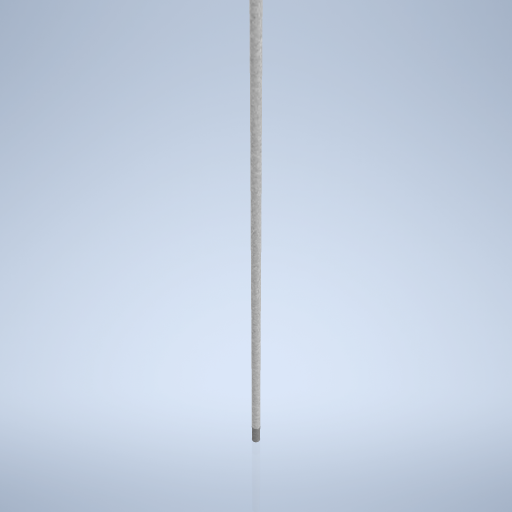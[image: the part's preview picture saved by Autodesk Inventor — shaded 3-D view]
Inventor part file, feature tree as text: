
AUTODESK INVENTOR PART (.ipt)
format: ipt  version: 2024.2 (Build 282272000, 272)  size: 262,144 bytes
history: native  units: mm
features: thread x2, revolve x1, sketch x1
ambient origin geometry x8: Origin, YZ Plane, XZ Plane, XY Plane, X Axis, Y Axis, Z Axis, Center Point
bodies: Volumenkörper1 (feature_tree)
feature tree (4):
  revolve  "Umdrehung1"
  thread  "Gewinde1"  [1 undecoded]
  thread  "Gewinde2"  [1 undecoded]
  sketch  "Skizze1"  dims[d3=6.0mm d4=7.5mm d5=360.0deg d6=10.5mm d7=0.0mm d8=18.0mm d9=0.0mm]
note: 2 required parameter values undecoded (feature->parameter linkage not recoverable at this tier; creation-order binding heuristic only, values carry confidence <= 0.55)
